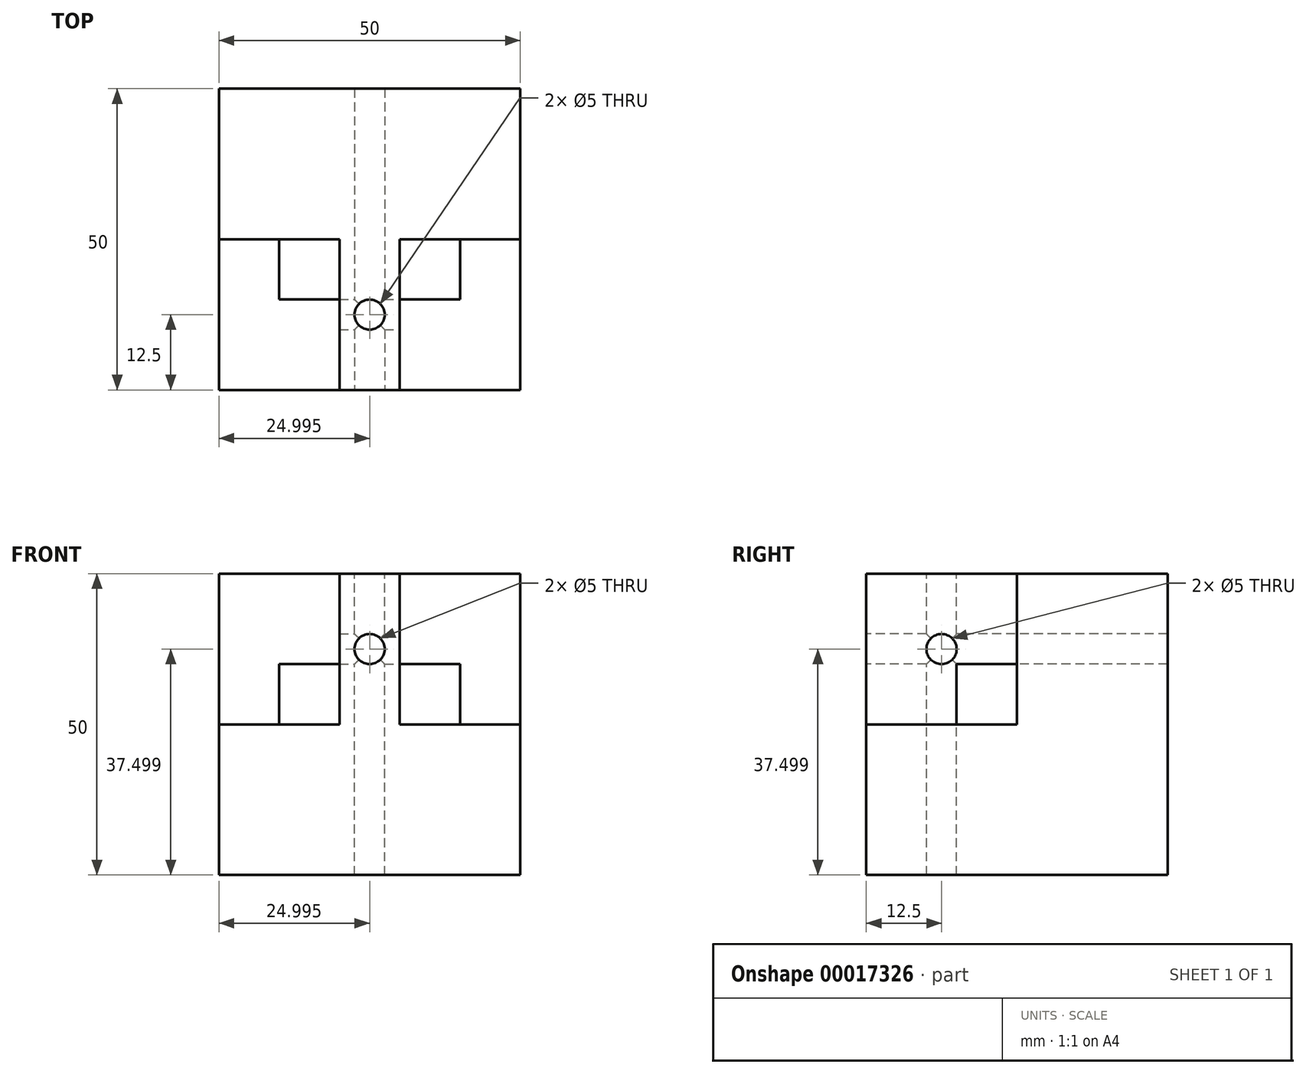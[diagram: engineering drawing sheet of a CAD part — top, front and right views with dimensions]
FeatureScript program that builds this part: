
annotation { "Feature Type Name" : "Feature", "Feature Type Description" : "" }
export const myFeature = defineFeature(function(context is Context, id is Id, definition is map)
    precondition{}
    {
        {
            var Q0;
            Q0=qCreatedBy(makeId("Front.planeOp"),FACE);
            var sketch = newSketch(context, id + "F0", { "sketchPlane" : qUnion([Q0])});
            skLineSegment(sketch, "E0.bottom", {"start": v(-34.61, 25.55) * mm, "end": v(15.39, 25.55) * mm});
            skLineSegment(sketch, "E0.top", {"start": v(-34.61, -24.45) * mm, "end": v(15.39, -24.45) * mm});
            skLineSegment(sketch, "E0.left", {"start": v(-34.61, 25.55) * mm, "end": v(-34.61, -24.45) * mm});
            skLineSegment(sketch, "E0.right", {"start": v(15.39, 25.55) * mm, "end": v(15.39, -24.45) * mm});
            skSolve(sketch);
        }
        {
            var Q0;
            Q0=makeQuery(id+"F0.imprint","IMPRINT",FACE,{"disambiguationData":[TD([[makeQuery(id+"F0.imprint","IMPRINT",EDGE,{"derivedFrom":sQuery(id+"F0.wireOp",EDGE,"E0.bottom")}),-1.0]])]});
            extrude(context, id + "F1", {"entities" : qUnion([Q0]), "oppositeDirection" : true, "depth" : 50 * mm});
        }
        {
            var Q0;
            Q0=makeQuery(id+"F1.opExtrude","CAP_FACE",FACE,{"disambiguationData":[OSD([sQuery(id+"F0.wireOp",EDGE,"E0.bottom"),sQuery(id+"F0.wireOp",EDGE,"E0.top"),sQuery(id+"F0.wireOp",EDGE,"E0.left"),sQuery(id+"F0.wireOp",EDGE,"E0.right")])],"isStart":true});
            var sketch = newSketch(context, id + "F2", { "sketchPlane" : qUnion([Q0])});
            skLineSegment(sketch, "E1", {"start": v(-34.61, 0.55) * mm, "end": v(-14.61, 0.55) * mm});
            skLineSegment(sketch, "E2", {"start": v(-14.61, 0.55) * mm, "end": v(-14.61, 25.55) * mm});
            skLineSegment(sketch, "E3", {"start": v(-14.61, 25.55) * mm, "end": v(-4.61, 25.55) * mm});
            skLineSegment(sketch, "E4", {"start": v(-4.61, 25.55) * mm, "end": v(-4.61, 0.55) * mm});
            skLineSegment(sketch, "E5", {"start": v(-4.61, 0.55) * mm, "end": v(15.39, 0.55) * mm});
            skLineSegment(sketch, "E6", {"start": v(15.39, 0.55) * mm, "end": v(15.39, 25.55) * mm});
            skLineSegment(sketch, "E7", {"start": v(15.39, 25.55) * mm, "end": v(-4.61, 25.55) * mm});
            skLineSegment(sketch, "E8", {"start": v(-34.61, 25.55) * mm, "end": v(-34.61, 0.55) * mm});
            skLineSegment(sketch, "E9", {"start": v(-34.61, 25.55) * mm, "end": v(-14.61, 25.55) * mm});
            skSolve(sketch);
        }
        {
            var Q0;
            Q0=makeQuery(id+"F2.imprint","IMPRINT",FACE,{"disambiguationData":[TD([[makeQuery(id+"F2.imprint","IMPRINT",EDGE,{"derivedFrom":sQuery(id+"F2.wireOp",EDGE,"E1")}),1.0]])]});
            var Q1;
            Q1=makeQuery(id+"F2.imprint","IMPRINT",FACE,{"disambiguationData":[TD([[makeQuery(id+"F2.imprint","IMPRINT",EDGE,{"derivedFrom":sQuery(id+"F2.wireOp",EDGE,"E4")}),1.0]])]});
            extrude(context, id + "F3", {"entities" : qUnion([Q0, Q1]), "operationType" : NewBodyOperationType.REMOVE, "oppositeDirection" : true, "depth" : 25 * mm});
        }
        {
            var Q0;
            Q0=makeQuery(id+"F1.opExtrude","CAP_FACE",FACE,{"disambiguationData":[OSD([sQuery(id+"F0.wireOp",EDGE,"E0.bottom"),sQuery(id+"F0.wireOp",EDGE,"E0.top"),sQuery(id+"F0.wireOp",EDGE,"E0.left"),sQuery(id+"F0.wireOp",EDGE,"E0.right")])],"isStart":true});
            var sketch = newSketch(context, id + "F4", { "sketchPlane" : qUnion([Q0])});
            skPoint(sketch, "E10", {"position": v(-9.61, 13.05) * mm});
            skSolve(sketch);
        }
        {
            var Q0;
            Q0=sQuery(id+"F4.wireOp",VERTEX,"E10");
            var Q1;
            Q1=makeQuery(id+"F1.opExtrude","SWEPT_BODY",BODY,{"disambiguationData":[OSD([sQuery(id+"F0.wireOp",EDGE,"E0.bottom"),sQuery(id+"F0.wireOp",EDGE,"E0.top"),sQuery(id+"F0.wireOp",EDGE,"E0.left"),sQuery(id+"F0.wireOp",EDGE,"E0.right")])]});
            hole(context, id + "F5", {"style" : HoleStyle.SIMPLE, "holeDiameter" : 5 * mm, "endStyle" : HoleEndStyle.THROUGH, "locations" : qUnion([Q0]), "scope" : qUnion([Q1])});
        }
        {
            var Q0;
            Q0=makeQuery(id+"F3.boolean.opBoolean","COPY",FACE,{"derivedFrom":makeQuery(id+"F3.opExtrude","SWEPT_FACE",FACE,{"disambiguationData":[OSD([sQuery(id+"F2.wireOp",EDGE,"E4")])]})});
            var sketch = newSketch(context, id + "F6", { "sketchPlane" : qUnion([Q0])});
            skPoint(sketch, "E11", {"position": v(12.5, 13.05) * mm});
            skSolve(sketch);
        }
        {
            var Q0;
            Q0=sQuery(id+"F6.wireOp",VERTEX,"E11");
            var Q1;
            Q1=makeQuery(id+"F1.opExtrude","SWEPT_BODY",BODY,{"disambiguationData":[OSD([sQuery(id+"F0.wireOp",EDGE,"E0.bottom"),sQuery(id+"F0.wireOp",EDGE,"E0.top"),sQuery(id+"F0.wireOp",EDGE,"E0.left"),sQuery(id+"F0.wireOp",EDGE,"E0.right")])]});
            hole(context, id + "F7", {"style" : HoleStyle.SIMPLE, "holeDiameter" : 5 * mm, "endStyle" : HoleEndStyle.THROUGH, "locations" : qUnion([Q0]), "scope" : qUnion([Q1])});
        }
        {
            var Q0;
            Q0=makeQuery(id+"F1.opExtrude","SWEPT_FACE",FACE,{"disambiguationData":[OSD([sQuery(id+"F0.wireOp",EDGE,"E0.bottom")])]});
            var sketch = newSketch(context, id + "F8", { "sketchPlane" : qUnion([Q0])});
            skPoint(sketch, "E12", {"position": v(-9.61, 12.5) * mm});
            skSolve(sketch);
        }
        {
            var Q0;
            Q0=sQuery(id+"F8.wireOp",VERTEX,"E12");
            var Q1;
            Q1=makeQuery(id+"F1.opExtrude","SWEPT_BODY",BODY,{"disambiguationData":[OSD([sQuery(id+"F0.wireOp",EDGE,"E0.bottom"),sQuery(id+"F0.wireOp",EDGE,"E0.top"),sQuery(id+"F0.wireOp",EDGE,"E0.left"),sQuery(id+"F0.wireOp",EDGE,"E0.right")])]});
            hole(context, id + "F9", {"style" : HoleStyle.SIMPLE, "holeDiameter" : 5 * mm, "endStyle" : HoleEndStyle.THROUGH, "locations" : qUnion([Q0]), "scope" : qUnion([Q1])});
        }
        {
            var Q0;
            Q0=makeQuery(id+"F3.boolean.opBoolean","COPY",FACE,{"derivedFrom":makeQuery(id+"F3.opExtrude","CAP_FACE",FACE,{"disambiguationData":[OSD([sQuery(id+"F2.wireOp",EDGE,"E4"),sQuery(id+"F2.wireOp",EDGE,"E5"),sQuery(id+"F2.wireOp",EDGE,"E6"),sQuery(id+"F2.wireOp",EDGE,"E7")])],"isStart":false})});
            var sketch = newSketch(context, id + "F10", { "sketchPlane" : qUnion([Q0])});
            skLineSegment(sketch, "E13.bottom", {"start": v(-4.61, 0.55) * mm, "end": v(5.39, 0.55) * mm});
            skLineSegment(sketch, "E13.top", {"start": v(-4.61, 10.55) * mm, "end": v(5.39, 10.55) * mm});
            skLineSegment(sketch, "E13.left", {"start": v(-4.61, 0.55) * mm, "end": v(-4.61, 10.55) * mm});
            skLineSegment(sketch, "E13.right", {"start": v(5.39, 0.55) * mm, "end": v(5.39, 10.55) * mm});
            skSolve(sketch);
        }
        {
            var Q0;
            Q0=makeQuery(id+"F10.imprint","IMPRINT",FACE,{"disambiguationData":[TD([[makeQuery(id+"F10.imprint","IMPRINT",EDGE,{"derivedFrom":sQuery(id+"F10.wireOp",EDGE,"E13.bottom")}),1.0]])]});
            extrude(context, id + "F11", {"entities" : qUnion([Q0]), "operationType" : NewBodyOperationType.ADD, "depth" : 10 * mm});
        }
        {
            var Q0;
            Q0=makeQuery(id+"F3.boolean.opBoolean","COPY",FACE,{"derivedFrom":makeQuery(id+"F3.opExtrude","CAP_FACE",FACE,{"disambiguationData":[OSD([sQuery(id+"F2.wireOp",EDGE,"E1"),sQuery(id+"F2.wireOp",EDGE,"E2"),sQuery(id+"F2.wireOp",EDGE,"E8"),sQuery(id+"F2.wireOp",EDGE,"E9")])],"isStart":false})});
            var sketch = newSketch(context, id + "F12", { "sketchPlane" : qUnion([Q0])});
            skLineSegment(sketch, "E14.bottom", {"start": v(-14.61, 0.55) * mm, "end": v(-24.61, 0.55) * mm});
            skLineSegment(sketch, "E14.top", {"start": v(-14.61, 10.55) * mm, "end": v(-24.61, 10.55) * mm});
            skLineSegment(sketch, "E14.left", {"start": v(-14.61, 0.55) * mm, "end": v(-14.61, 10.55) * mm});
            skLineSegment(sketch, "E14.right", {"start": v(-24.61, 0.55) * mm, "end": v(-24.61, 10.55) * mm});
            skSolve(sketch);
        }
        {
            var Q0;
            Q0=makeQuery(id+"F12.imprint","IMPRINT",FACE,{"disambiguationData":[TD([[makeQuery(id+"F12.imprint","IMPRINT",EDGE,{"derivedFrom":sQuery(id+"F12.wireOp",EDGE,"E14.bottom")}),1.0]])]});
            extrude(context, id + "F13", {"entities" : qUnion([Q0]), "operationType" : NewBodyOperationType.ADD, "depth" : 10 * mm});
        }
    });
